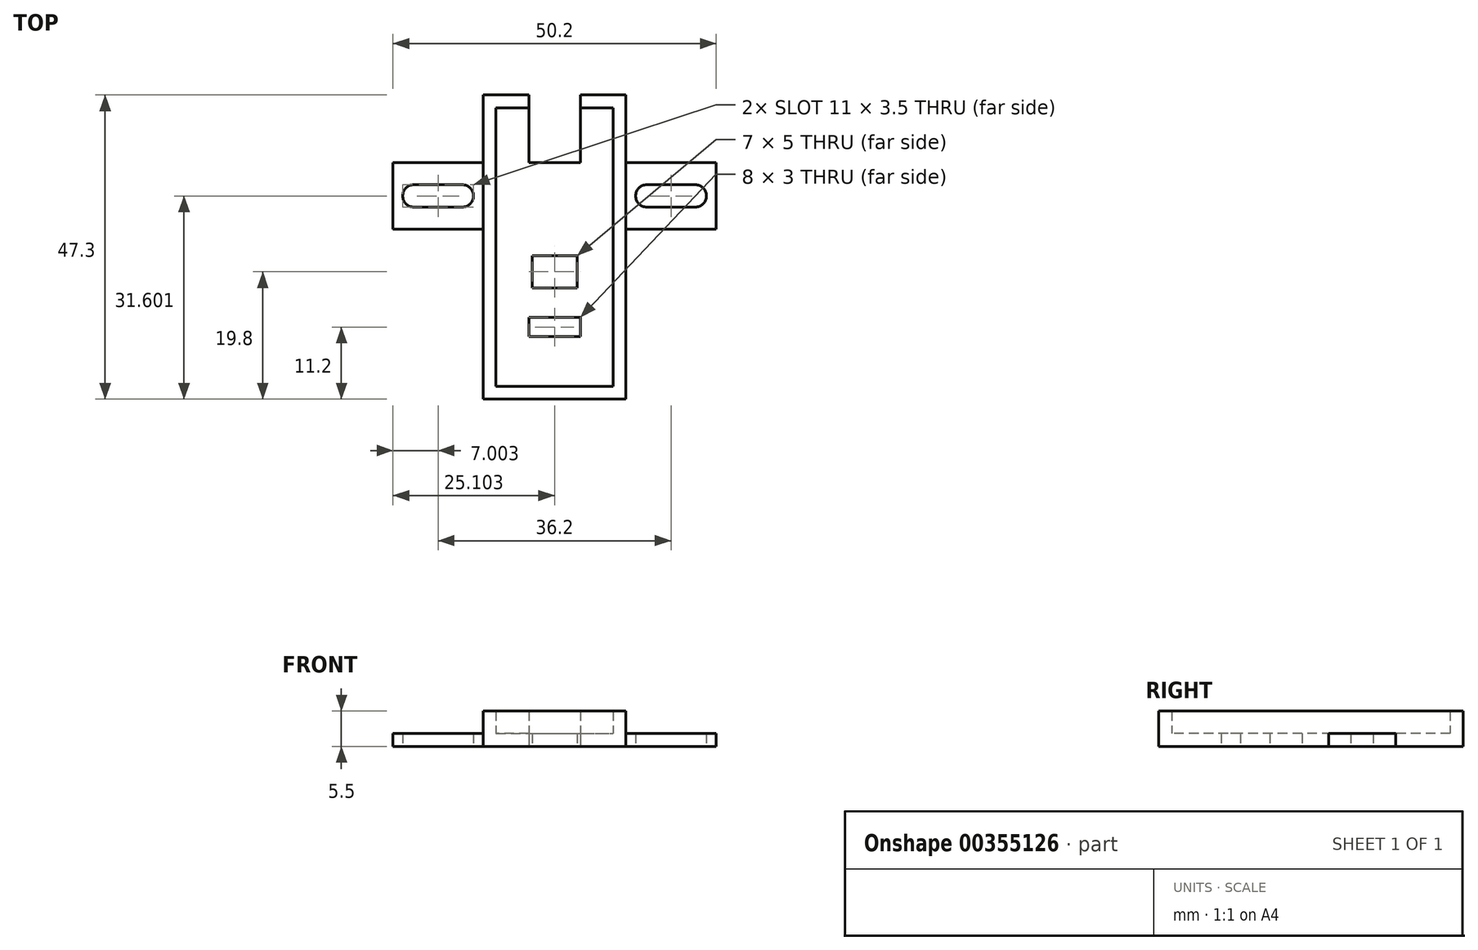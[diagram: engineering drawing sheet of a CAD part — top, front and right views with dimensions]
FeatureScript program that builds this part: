
annotation { "Feature Type Name" : "Feature", "Feature Type Description" : "" }
export const myFeature = defineFeature(function(context is Context, id is Id, definition is map)
    precondition{}
    {
        {
            var Q0;
            Q0=qCreatedBy(makeId("Top.planeOp"),FACE);
            var sketch = newSketch(context, id + "F0", { "sketchPlane" : qUnion([Q0])});
            skLineSegment(sketch, "E0", {"start": v(-14.6, 37.9) * mm, "end": v(-19.7, 37.9) * mm});
            skLineSegment(sketch, "E1", {"start": v(-19.7, 37.9) * mm, "end": v(-19.7, -5.4) * mm});
            skLineSegment(sketch, "E2", {"start": v(-10.6, 15.4) * mm, "end": v(-10.6, -7.96) * mm, "construction": true});
            skLineSegment(sketch, "E3", {"start": v(-19.7, -5.4) * mm, "end": v(-10.6, -5.4) * mm});
            skLineSegment(sketch, "E4", {"start": v(-14.6, 37.9) * mm, "end": v(-14.6, 29.4) * mm});
            skLineSegment(sketch, "E5", {"start": v(-14.6, 29.4) * mm, "end": v(-10.6, 29.4) * mm});
            skLineSegment(sketch, "E6.MirrorCS", {"start": v(-6.6, 29.4) * mm, "end": v(-10.6, 29.4) * mm});
            skLineSegment(sketch, "E7.MirrorCS", {"start": v(-6.6, 37.9) * mm, "end": v(-1.5, 37.9) * mm});
            skLineSegment(sketch, "E8.MirrorCS", {"start": v(-6.6, 37.9) * mm, "end": v(-6.6, 29.4) * mm});
            skLineSegment(sketch, "E9.MirrorCS", {"start": v(-1.5, -5.4) * mm, "end": v(-10.6, -5.4) * mm});
            skLineSegment(sketch, "E10.MirrorCS", {"start": v(-1.5, 37.9) * mm, "end": v(-1.5, -5.4) * mm});
            skLineSegment(sketch, "E11.bottom", {"start": v(-14.1, 14.9) * mm, "end": v(-7.1, 14.9) * mm});
            skLineSegment(sketch, "E11.top", {"start": v(-14.1, 9.9) * mm, "end": v(-7.1, 9.9) * mm});
            skLineSegment(sketch, "E11.left", {"start": v(-14.1, 14.9) * mm, "end": v(-14.1, 9.9) * mm});
            skLineSegment(sketch, "E11.right", {"start": v(-7.1, 14.9) * mm, "end": v(-7.1, 9.9) * mm});
            skPoint(sketch, "E11.middle", {"position": v(-10.6, 12.4) * mm});
            skLineSegment(sketch, "E12.bottom", {"start": v(-14.6, 5.3) * mm, "end": v(-6.6, 5.3) * mm});
            skLineSegment(sketch, "E12.top", {"start": v(-14.6, 2.3) * mm, "end": v(-6.6, 2.3) * mm});
            skLineSegment(sketch, "E12.left", {"start": v(-14.6, 5.3) * mm, "end": v(-14.6, 2.3) * mm});
            skLineSegment(sketch, "E12.right", {"start": v(-6.6, 5.3) * mm, "end": v(-6.6, 2.3) * mm});
            skPoint(sketch, "E12.middle", {"position": v(-10.6, 3.8) * mm});
            skLineSegment(sketch, "E13.0", {"start": v(-14.6, 39.9) * mm, "end": v(-21.7, 39.9) * mm});
            skLineSegment(sketch, "E13.1", {"start": v(-21.7, 39.9) * mm, "end": v(-21.7, -7.4) * mm});
            skLineSegment(sketch, "E13.2", {"start": v(-6.6, 39.9) * mm, "end": v(0.5, 39.9) * mm});
            skLineSegment(sketch, "E13.3", {"start": v(0.5, 39.9) * mm, "end": v(0.5, -7.4) * mm});
            skLineSegment(sketch, "E13.4", {"start": v(0.5, -7.4) * mm, "end": v(-10.6, -7.4) * mm});
            skLineSegment(sketch, "E13.5", {"start": v(-21.7, -7.4) * mm, "end": v(-10.6, -7.4) * mm});
            skLineSegment(sketch, "E14", {"start": v(-6.6, 39.9) * mm, "end": v(-6.6, 37.9) * mm});
            skLineSegment(sketch, "E15", {"start": v(-14.6, 39.9) * mm, "end": v(-14.6, 37.9) * mm});
            skLineSegment(sketch, "E16", {"start": v(-6.6, 29.4) * mm, "end": v(17.75, 29.4) * mm, "construction": true});
            skLineSegment(sketch, "E17.bottom", {"start": v(0.5, 29.4) * mm, "end": v(14.5, 29.4) * mm});
            skLineSegment(sketch, "E17.top", {"start": v(0.5, 19) * mm, "end": v(14.5, 19) * mm});
            skLineSegment(sketch, "E17.left", {"start": v(0.5, 29.4) * mm, "end": v(0.5, 19) * mm});
            skLineSegment(sketch, "E17.right", {"start": v(14.5, 29.4) * mm, "end": v(14.5, 19) * mm});
            skLineSegment(sketch, "E18", {"start": v(14.5, 24.2) * mm, "end": v(31.97, 24.2) * mm, "construction": true});
            skCircle(sketch, "E19", {"center": v(11.24, 24.2) * mm, "radius": 1.75 * mm});
            skLineSegment(sketch, "E20", {"start": v(7.5, 19) * mm, "end": v(7.5, 25.9) * mm, "construction": true});
            skCircle(sketch, "E21.MirrorC", {"center": v(3.74, 24.2) * mm, "radius": 1.75 * mm});
            skLineSegment(sketch, "E22", {"start": v(11.24, 25.94) * mm, "end": v(3.74, 25.94) * mm});
            skLineSegment(sketch, "E23", {"start": v(3.74, 22.44) * mm, "end": v(11.24, 22.44) * mm});
            skPoint(sketch, "E23.endSnap0", {"position": v(7.5, 22.44) * mm});
            skLineSegment(sketch, "E24.MirrorCS", {"start": v(-21.7, 29.4) * mm, "end": v(-35.7, 29.4) * mm});
            skPoint(sketch, "E25.MirrorP", {"position": v(-28.7, 22.44) * mm});
            skLineSegment(sketch, "E26.MirrorCS", {"start": v(-21.7, 29.4) * mm, "end": v(-21.7, 19) * mm});
            skCircle(sketch, "E27.MirrorC", {"center": v(-32.46, 24.2) * mm, "radius": 1.75 * mm});
            skLineSegment(sketch, "E28.MirrorCS", {"start": v(-35.7, 29.4) * mm, "end": v(-35.7, 19) * mm});
            skLineSegment(sketch, "E29.MirrorCS", {"start": v(-21.7, 19) * mm, "end": v(-35.7, 19) * mm});
            skLineSegment(sketch, "E30.MirrorCS", {"start": v(-24.96, 22.44) * mm, "end": v(-32.46, 22.44) * mm});
            skCircle(sketch, "E31.MirrorC", {"center": v(-24.96, 24.2) * mm, "radius": 1.75 * mm});
            skLineSegment(sketch, "E32.MirrorCS", {"start": v(-32.46, 25.94) * mm, "end": v(-24.96, 25.94) * mm});
            skSolve(sketch);
        }
        {
            var Q0;
            Q0=makeQuery(id+"F0.imprint","IMPRINT",FACE,{"disambiguationData":[TD([[makeQuery(id+"F0.imprint","IMPRINT",EDGE,{"derivedFrom":sQuery(id+"F0.wireOp",EDGE,"E0")}),1.0]])]});
            var Q1;
            Q1=makeQuery(id+"F0.imprint","IMPRINT",FACE,{"disambiguationData":[TD([[makeQuery(id+"F0.imprint","IMPRINT",EDGE,{"derivedFrom":sQuery(id+"F0.wireOp",EDGE,"E17.bottom")}),-1.0]])]});
            var Q2;
            Q2=makeQuery(id+"F0.imprint","IMPRINT",FACE,{"disambiguationData":[TD([[makeQuery(id+"F0.imprint","IMPRINT",EDGE,{"derivedFrom":sQuery(id+"F0.wireOp",EDGE,"E24.MirrorCS")}),1.0]])]});
            extrude(context, id + "F1", {"entities" : qUnion([Q0, Q1, Q2]), "depth" : 2 * mm});
        }
        {
            var Q0;
            Q0=makeQuery(id+"F0.imprint","IMPRINT",FACE,{"disambiguationData":[TD([[makeQuery(id+"F0.imprint","IMPRINT",EDGE,{"derivedFrom":sQuery(id+"F0.wireOp",EDGE,"E0")}),-1.0]])]});
            extrude(context, id + "F2", {"entities" : qUnion([Q0]), "operationType" : NewBodyOperationType.ADD, "depth" : 5.5 * mm});
        }
    });
